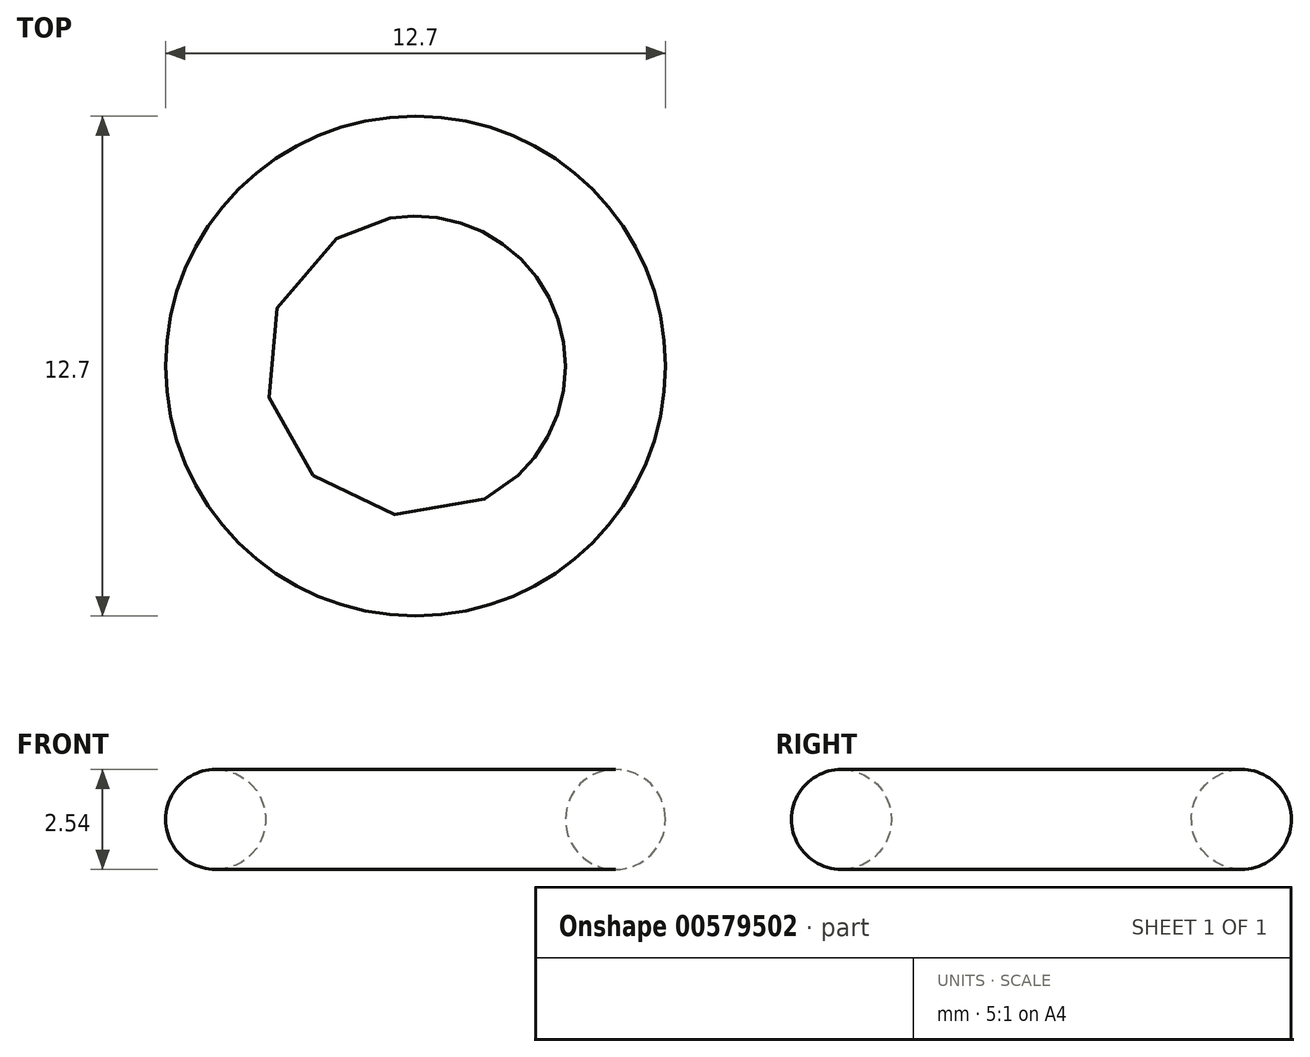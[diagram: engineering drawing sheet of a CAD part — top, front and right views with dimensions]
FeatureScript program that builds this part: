
annotation { "Feature Type Name" : "Feature", "Feature Type Description" : "" }
export const myFeature = defineFeature(function(context is Context, id is Id, definition is map)
    precondition{}
    {
        {
            var Q0;
            Q0=qCreatedBy(makeId("Top.planeOp"),FACE);
            var sketch = newSketch(context, id + "F0", { "sketchPlane" : qUnion([Q0])});
            skCircle(sketch, "E0", {"center": v(0, 0) * mm, "radius": 6.35 * mm});
            skCircle(sketch, "E1", {"center": v(0, 0) * mm, "radius": 3.81 * mm});
            skSolve(sketch);
        }
        {
            var Q0;
            Q0=makeQuery(id+"F0.imprint","IMPRINT",FACE,{"disambiguationData":[TD([[makeQuery(id+"F0.imprint","IMPRINT",EDGE,{"derivedFrom":sQuery(id+"F0.wireOp",EDGE,"E0")}),1.0]])]});
            extrude(context, id + "F1", {"entities" : qUnion([Q0]), "depth" : 2.54 * mm, "offsetDistance" : 25.4 * mm});
        }
        {
            var Q0;
            Q0=makeQuery(id+"F1.opExtrude","CAP_EDGE",EDGE,{"disambiguationData":[OSD([sQuery(id+"F0.wireOp",EDGE,"E0")])],"isStart":false});
            var Q1;
            Q1=makeQuery(id+"F1.opExtrude","CAP_EDGE",EDGE,{"disambiguationData":[OSD([sQuery(id+"F0.wireOp",EDGE,"E0")])],"isStart":true});
            var Q2;
            Q2=makeQuery(id+"F1.opExtrude","CAP_EDGE",EDGE,{"disambiguationData":[OSD([sQuery(id+"F0.wireOp",EDGE,"E1")])],"isStart":false});
            var Q3;
            Q3=makeQuery(id+"F1.opExtrude","CAP_EDGE",EDGE,{"disambiguationData":[OSD([sQuery(id+"F0.wireOp",EDGE,"E1")])],"isStart":true});
            fillet(context, id + "F2", {"entities" : qUnion([Q0, Q1, Q2, Q3]), "radius" : 1.27 * mm, "tangentPropagation" : true, "allowEdgeOverflow" : false});
        }
    });
